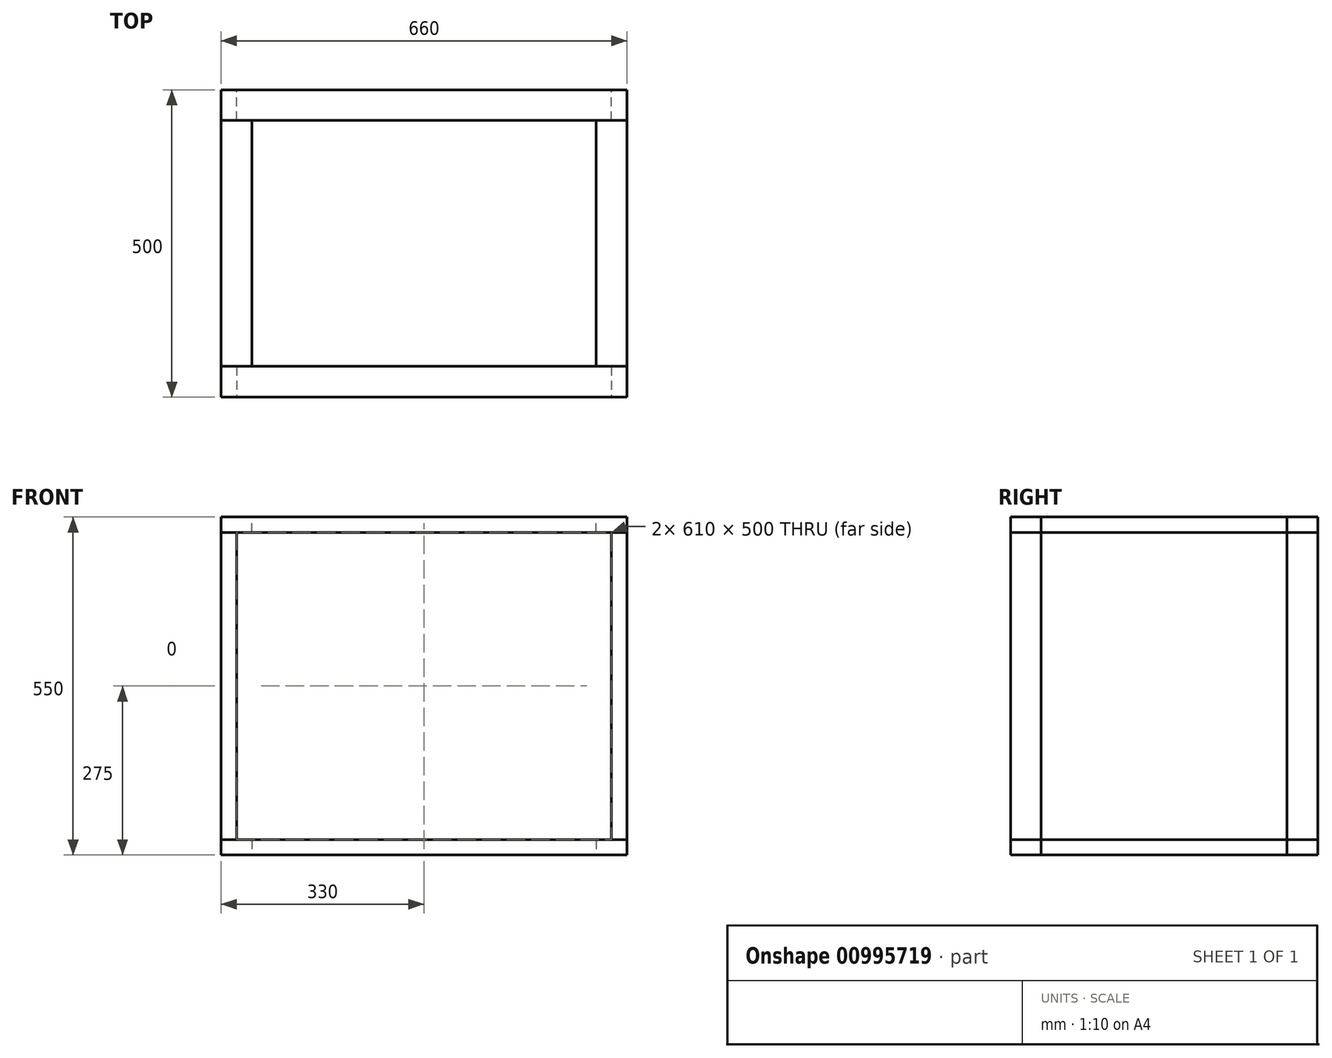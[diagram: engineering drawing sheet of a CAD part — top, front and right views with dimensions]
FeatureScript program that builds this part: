
annotation { "Feature Type Name" : "Feature", "Feature Type Description" : "" }
export const myFeature = defineFeature(function(context is Context, id is Id, definition is map)
    precondition{}
    {
        {
            var Q0;
            Q0=qCreatedBy(makeId("Top.planeOp"),FACE);
            cPlane(context, id + "F0", {"entities" : qUnion([Q0]), "cplaneType" : CPlaneType.OFFSET, "offset" : 275 * mm, "width" : 150 * mm, "height" : 150 * mm});
        }
        {
            var Q0;
            Q0=qCreatedBy(id+"F0.planeOp",FACE);
            var sketch = newSketch(context, id + "F1", { "sketchPlane" : qUnion([Q0])});
            skLineSegment(sketch, "E0.bottom", {"start": v(330, 250) * mm, "end": v(-330, 250) * mm});
            skLineSegment(sketch, "E0.top", {"start": v(330, -250) * mm, "end": v(-330, -250) * mm});
            skLineSegment(sketch, "E0.left", {"start": v(330, 250) * mm, "end": v(330, -250) * mm});
            skLineSegment(sketch, "E0.right", {"start": v(-330, 250) * mm, "end": v(-330, -250) * mm});
            skPoint(sketch, "E0.middle", {"position": v(0, 0) * mm});
            skLineSegment(sketch, "E1.bottom", {"start": v(280, 200) * mm, "end": v(-280, 200) * mm});
            skLineSegment(sketch, "E1.top", {"start": v(280, -200) * mm, "end": v(-280, -200) * mm});
            skLineSegment(sketch, "E1.left", {"start": v(280, 200) * mm, "end": v(280, -200) * mm});
            skLineSegment(sketch, "E1.right", {"start": v(-280, 200) * mm, "end": v(-280, -200) * mm});
            skSolve(sketch);
        }
        {
            var Q0;
            Q0 = qSketchRegion(id + "F1", true);
            extrude(context, id + "F2", {"entities" : qUnion([Q0]), "oppositeDirection" : true, "depth" : 25 * mm, "offsetDistance" : 25 * mm});
        }
        {
            var Q0;
            Q0=qCreatedBy(makeId("Top.planeOp"),FACE);
            cPlane(context, id + "F3", {"entities" : qUnion([Q0]), "cplaneType" : CPlaneType.OFFSET, "offset" : 275 * mm, "oppositeDirection" : true, "width" : 150 * mm, "height" : 150 * mm});
        }
        {
            var Q0;
            Q0=qCreatedBy(id+"F3.planeOp",FACE);
            var sketch = newSketch(context, id + "F4", { "sketchPlane" : qUnion([Q0])});
            skLineSegment(sketch, "E2.bottom", {"start": v(330, 250) * mm, "end": v(-330, 250) * mm});
            skLineSegment(sketch, "E2.top", {"start": v(330, -250) * mm, "end": v(-330, -250) * mm});
            skLineSegment(sketch, "E2.left", {"start": v(330, 250) * mm, "end": v(330, -250) * mm});
            skLineSegment(sketch, "E2.right", {"start": v(-330, 250) * mm, "end": v(-330, -250) * mm});
            skPoint(sketch, "E2.middle", {"position": v(0, 0) * mm});
            skLineSegment(sketch, "E3.bottom", {"start": v(280, 200) * mm, "end": v(-280, 200) * mm});
            skLineSegment(sketch, "E3.top", {"start": v(280, -200) * mm, "end": v(-280, -200) * mm});
            skLineSegment(sketch, "E3.left", {"start": v(280, 200) * mm, "end": v(280, -200) * mm});
            skLineSegment(sketch, "E3.right", {"start": v(-280, 200) * mm, "end": v(-280, -200) * mm});
            skSolve(sketch);
        }
        {
            var Q0;
            Q0 = qSketchRegion(id + "F4", true);
            extrude(context, id + "F5", {"entities" : qUnion([Q0]), "depth" : 25 * mm, "offsetDistance" : 25 * mm});
        }
        {
            var Q0;
            Q0=qCreatedBy(makeId("Front.planeOp"),FACE);
            cPlane(context, id + "F6", {"entities" : qUnion([Q0]), "cplaneType" : CPlaneType.OFFSET, "offset" : 250 * mm, "width" : 150 * mm, "height" : 150 * mm});
        }
        {
            var Q0;
            Q0=qCreatedBy(makeId("Front.planeOp"),FACE);
            cPlane(context, id + "F7", {"entities" : qUnion([Q0]), "cplaneType" : CPlaneType.OFFSET, "offset" : 250 * mm, "oppositeDirection" : true, "width" : 150 * mm, "height" : 150 * mm});
        }
        {
            var Q0;
            Q0=qCreatedBy(id+"F6.planeOp",FACE);
            var sketch = newSketch(context, id + "F8", { "sketchPlane" : qUnion([Q0])});
            skLineSegment(sketch, "E4.bottom", {"start": v(-330, 275) * mm, "end": v(330, 275) * mm});
            skLineSegment(sketch, "E4.top", {"start": v(-330, -275) * mm, "end": v(330, -275) * mm});
            skLineSegment(sketch, "E4.left", {"start": v(-330, 275) * mm, "end": v(-330, -275) * mm});
            skLineSegment(sketch, "E4.right", {"start": v(330, 275) * mm, "end": v(330, -275) * mm});
            skPoint(sketch, "E4.middle", {"position": v(0, 0) * mm});
            skLineSegment(sketch, "E5.bottom", {"start": v(-305, 250) * mm, "end": v(305, 250) * mm});
            skLineSegment(sketch, "E5.top", {"start": v(-305, -250) * mm, "end": v(305, -250) * mm});
            skLineSegment(sketch, "E5.left", {"start": v(-305, 250) * mm, "end": v(-305, -250) * mm});
            skLineSegment(sketch, "E5.right", {"start": v(305, 250) * mm, "end": v(305, -250) * mm});
            skSolve(sketch);
        }
        {
            var Q0;
            Q0 = qSketchRegion(id + "F8", true);
            extrude(context, id + "F9", {"entities" : qUnion([Q0]), "oppositeDirection" : true, "depth" : 50 * mm, "offsetDistance" : 25 * mm});
        }
        {
            var Q0;
            Q0=qCreatedBy(id+"F7.planeOp",FACE);
            var sketch = newSketch(context, id + "F10", { "sketchPlane" : qUnion([Q0])});
            skLineSegment(sketch, "E6.bottom", {"start": v(-330, 275) * mm, "end": v(330, 275) * mm});
            skLineSegment(sketch, "E6.top", {"start": v(-330, -275) * mm, "end": v(330, -275) * mm});
            skLineSegment(sketch, "E6.left", {"start": v(-330, 275) * mm, "end": v(-330, -275) * mm});
            skLineSegment(sketch, "E6.right", {"start": v(330, 275) * mm, "end": v(330, -275) * mm});
            skPoint(sketch, "E6.middle", {"position": v(0, 0) * mm});
            skLineSegment(sketch, "E7.bottom", {"start": v(-305, 250) * mm, "end": v(305, 250) * mm});
            skLineSegment(sketch, "E7.top", {"start": v(-305, -250) * mm, "end": v(305, -250) * mm});
            skLineSegment(sketch, "E7.left", {"start": v(-305, 250) * mm, "end": v(-305, -250) * mm});
            skLineSegment(sketch, "E7.right", {"start": v(305, 250) * mm, "end": v(305, -250) * mm});
            skSolve(sketch);
        }
        {
            var Q0;
            Q0 = qSketchRegion(id + "F10", true);
            extrude(context, id + "F11", {"entities" : qUnion([Q0]), "depth" : 50 * mm, "offsetDistance" : 25 * mm});
        }
    });
